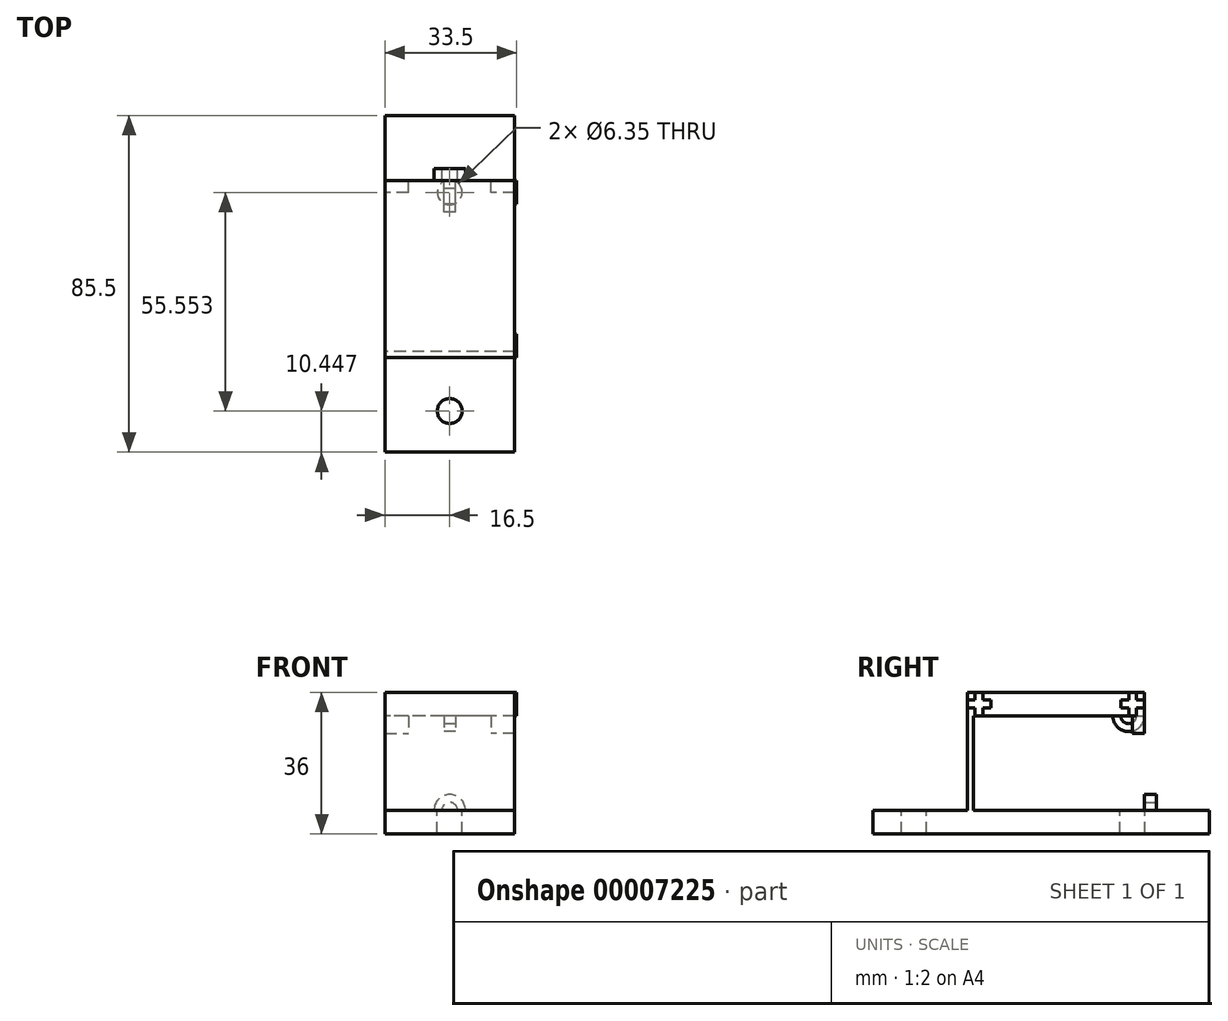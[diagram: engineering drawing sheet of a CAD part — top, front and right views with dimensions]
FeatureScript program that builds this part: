
annotation { "Feature Type Name" : "Feature", "Feature Type Description" : "" }
export const myFeature = defineFeature(function(context is Context, id is Id, definition is map)
    precondition{}
    {
        {
            var Q0;
            Q0=qCreatedBy(makeId("Right.planeOp"),FACE);
            var sketch = newSketch(context, id + "F0", { "sketchPlane" : qUnion([Q0])});
            skLineSegment(sketch, "E0", {"start": v(1.5, 30) * mm, "end": v(42, 30) * mm});
            skLineSegment(sketch, "E1", {"start": v(45, 30) * mm, "end": v(45, 36) * mm});
            skLineSegment(sketch, "E2", {"start": v(45, 36) * mm, "end": v(0, 36) * mm});
            skLineSegment(sketch, "E3", {"start": v(0, 36) * mm, "end": v(0, 6) * mm});
            skLineSegment(sketch, "E4", {"start": v(0, 0) * mm, "end": v(61.5, 0) * mm});
            skLineSegment(sketch, "E5", {"start": v(1.5, 30) * mm, "end": v(1.5, 6) * mm});
            skLineSegment(sketch, "E6", {"start": v(1.5, 6) * mm, "end": v(61.5, 6) * mm});
            skLineSegment(sketch, "E7", {"start": v(61.5, 6) * mm, "end": v(61.5, 0) * mm});
            skPoint(sketch, "E8", {"position": v(42, 30) * mm});
            skPoint(sketch, "E9", {"position": v(0, 30) * mm});
            skPoint(sketch, "E10", {"position": v(0, 6) * mm});
            skLineSegment(sketch, "E11", {"start": v(0, 6) * mm, "end": v(-24, 6) * mm});
            skLineSegment(sketch, "E12", {"start": v(-24, 6) * mm, "end": v(-24, 0) * mm});
            skLineSegment(sketch, "E13", {"start": v(-24, 0) * mm, "end": v(0, 0) * mm});
            skPoint(sketch, "E14.end.orphan", {"position": v(45, 22.38) * mm});
            skLineSegment(sketch, "E15", {"start": v(42, 30) * mm, "end": v(45, 30) * mm});
            skSolve(sketch);
        }
        {
            var Q0;
            Q0=qSketchRegion(id+"F0",true);
            extrude(context, id + "F1", {"entities" : qUnion([Q0]), "depth" : 33 * mm});
        }
        {
            var Q0;
            Q0=makeQuery(id+"F1.opExtrude","CAP_FACE",FACE,{"disambiguationData":[OSD([sQuery(id+"F0.wireOp",EDGE,"E0"),sQuery(id+"F0.wireOp",EDGE,"E1"),sQuery(id+"F0.wireOp",EDGE,"E2"),sQuery(id+"F0.wireOp",EDGE,"E3"),sQuery(id+"F0.wireOp",EDGE,"E4"),sQuery(id+"F0.wireOp",EDGE,"E5"),sQuery(id+"F0.wireOp",EDGE,"E6"),sQuery(id+"F0.wireOp",EDGE,"E7"),sQuery(id+"F0.wireOp",EDGE,"E11"),sQuery(id+"F0.wireOp",EDGE,"E12"),sQuery(id+"F0.wireOp",EDGE,"E13"),sQuery(id+"F0.wireOp",EDGE,"E15")])],"isStart":false});
            var sketch = newSketch(context, id + "F2", { "sketchPlane" : qUnion([Q0])});
            skArc(sketch, "E16", {"start": v(37, 30) * mm, "mid": v(41, 26) * mm, "end": v(45, 30) * mm});
            skArc(sketch, "E17", {"start": v(39, 30) * mm, "mid": v(41, 28) * mm, "end": v(43, 30) * mm});
            skLineSegment(sketch, "E18", {"start": v(39, 30) * mm, "end": v(37, 30) * mm});
            skLineSegment(sketch, "E19", {"start": v(37, 30) * mm, "end": v(39, 30) * mm});
            skLineSegment(sketch, "E20", {"start": v(43, 30) * mm, "end": v(45, 30) * mm});
            skSolve(sketch);
        }
        {
            var Q0;
            Q0 = qSketchRegion(id + "F2", true);
            extrude(context, id + "F3", {"entities" : qUnion([Q0]), "depth" : 3 * mm});
        }
        {
            var Q0;
            Q0=makeQuery(id+"F3.opExtrude","SWEPT_BODY",BODY,{"disambiguationData":[OSD([sQuery(id+"F2.wireOp",EDGE,"E16"),sQuery(id+"F2.wireOp",EDGE,"E17"),sQuery(id+"F2.wireOp",EDGE,"E19"),sQuery(id+"F2.wireOp",EDGE,"E20")])]});
            var Q1;
            Q1=makeQuery(id+"F1.opExtrude","SWEPT_EDGE",EDGE,{"disambiguationData":[OSD([sQuery(id+"F0.wireOp",EDGE,"E1"),sQuery(id+"F0.wireOp",EDGE,"E15")])]});
            transform(context, id + "F4", {"entities" : qUnion([Q0]), "transformType" : TransformType.TRANSLATION_DISTANCE, "transformDirection" : qUnion([Q1]), "distance" : 18 * mm, "makeCopy" : false});
        }
        {
            var Q0;
            Q0=makeQuery(id+"F1.opExtrude","SWEPT_FACE",FACE,{"disambiguationData":[OSD([sQuery(id+"F0.wireOp",EDGE,"E7")])]});
            var sketch = newSketch(context, id + "F5", { "sketchPlane" : qUnion([Q0])});
            skArc(sketch, "E21", {"start": v(-12.5, 6) * mm, "mid": v(-16.5, 10) * mm, "end": v(-20.5, 6) * mm});
            skArc(sketch, "E22", {"start": v(-14.5, 6) * mm, "mid": v(-16.5, 8) * mm, "end": v(-18.5, 6) * mm});
            skLineSegment(sketch, "E23", {"start": v(-20.5, 6) * mm, "end": v(-18.5, 6) * mm});
            skLineSegment(sketch, "E24", {"start": v(-14.5, 6) * mm, "end": v(-12.5, 6) * mm});
            skSolve(sketch);
        }
        {
            var Q0;
            Q0 = qSketchRegion(id + "F5", true);
            extrude(context, id + "F6", {"entities" : qUnion([Q0]), "oppositeDirection" : true, "depth" : 3 * mm});
        }
        {
            var Q0;
            Q0=makeQuery(id+"F6.opExtrude","SWEPT_BODY",BODY,{"disambiguationData":[OSD([sQuery(id+"F5.wireOp",EDGE,"E21"),sQuery(id+"F5.wireOp",EDGE,"E22"),sQuery(id+"F5.wireOp",EDGE,"E23"),sQuery(id+"F5.wireOp",EDGE,"E24")])]});
            var Q1;
            Q1=makeQuery(id+"F1.opExtrude","CAP_EDGE",EDGE,{"disambiguationData":[OSD([sQuery(id+"F0.wireOp",EDGE,"E6")])],"isStart":false});
            transform(context, id + "F7", {"entities" : qUnion([Q0]), "transformType" : TransformType.TRANSLATION_DISTANCE, "transformDirection" : qUnion([Q1]), "distance" : 13.5 * mm, "oppositeDirection" : true, "makeCopy" : false});
        }
        {
            var Q0;
            Q0=makeQuery(id+"F1.opExtrude","SWEPT_FACE",FACE,{"disambiguationData":[OSD([sQuery(id+"F0.wireOp",EDGE,"E1")])]});
            var sketch = newSketch(context, id + "F8", { "sketchPlane" : qUnion([Q0])});
            skLineSegment(sketch, "E25.bottom", {"start": v(-33, 30) * mm, "end": v(-27, 30) * mm});
            skLineSegment(sketch, "E25.top", {"start": v(-33, 25.5) * mm, "end": v(-27, 25.5) * mm});
            skLineSegment(sketch, "E25.left", {"start": v(-33, 30) * mm, "end": v(-33, 25.5) * mm});
            skLineSegment(sketch, "E25.right", {"start": v(-27, 30) * mm, "end": v(-27, 25.5) * mm});
            skLineSegment(sketch, "E26.bottom", {"start": v(0, 30) * mm, "end": v(-6, 30) * mm});
            skLineSegment(sketch, "E26.top", {"start": v(0, 25.5) * mm, "end": v(-6, 25.5) * mm});
            skLineSegment(sketch, "E26.left", {"start": v(0, 30) * mm, "end": v(0, 25.5) * mm});
            skLineSegment(sketch, "E26.right", {"start": v(-6, 30) * mm, "end": v(-6, 25.5) * mm});
            skLineSegment(sketch, "E27", {"start": v(-16.5, 30) * mm, "end": v(-16.5, 12.44) * mm, "construction": true});
            skSolve(sketch);
        }
        {
            var Q0;
            Q0 = qSketchRegion(id + "F8", true);
            extrude(context, id + "F9", {"entities" : qUnion([Q0]), "oppositeDirection" : true, "depth" : 3 * mm});
        }
        {
            var Q0;
            Q0=makeQuery(id+"F1.opExtrude","SWEPT_BODY",BODY,{"disambiguationData":[OSD([sQuery(id+"F0.wireOp",EDGE,"E0"),sQuery(id+"F0.wireOp",EDGE,"E1"),sQuery(id+"F0.wireOp",EDGE,"E2"),sQuery(id+"F0.wireOp",EDGE,"E3"),sQuery(id+"F0.wireOp",EDGE,"E4"),sQuery(id+"F0.wireOp",EDGE,"E5"),sQuery(id+"F0.wireOp",EDGE,"E6"),sQuery(id+"F0.wireOp",EDGE,"E7"),sQuery(id+"F0.wireOp",EDGE,"E11"),sQuery(id+"F0.wireOp",EDGE,"E12"),sQuery(id+"F0.wireOp",EDGE,"E13"),sQuery(id+"F0.wireOp",EDGE,"E15")])]});
            var Q1;
            Q1=makeQuery(id+"F3.opExtrude","SWEPT_BODY",BODY,{"disambiguationData":[OSD([sQuery(id+"F2.wireOp",EDGE,"E16"),sQuery(id+"F2.wireOp",EDGE,"E17"),sQuery(id+"F2.wireOp",EDGE,"E19"),sQuery(id+"F2.wireOp",EDGE,"E20")])]});
            var Q2;
            Q2=makeQuery(id+"F9.opExtrude","SWEPT_BODY",BODY,{"disambiguationData":[OSD([sQuery(id+"F8.wireOp",EDGE,"E26.bottom"),sQuery(id+"F8.wireOp",EDGE,"E26.top"),sQuery(id+"F8.wireOp",EDGE,"E26.left"),sQuery(id+"F8.wireOp",EDGE,"E26.right")])]});
            var Q3;
            Q3=makeQuery(id+"F9.opExtrude","SWEPT_BODY",BODY,{"disambiguationData":[OSD([sQuery(id+"F8.wireOp",EDGE,"E25.bottom"),sQuery(id+"F8.wireOp",EDGE,"E25.top"),sQuery(id+"F8.wireOp",EDGE,"E25.left"),sQuery(id+"F8.wireOp",EDGE,"E25.right")])]});
            var Q4;
            Q4=makeQuery(id+"F6.opExtrude","SWEPT_BODY",BODY,{"disambiguationData":[OSD([sQuery(id+"F5.wireOp",EDGE,"E21"),sQuery(id+"F5.wireOp",EDGE,"E22"),sQuery(id+"F5.wireOp",EDGE,"E23"),sQuery(id+"F5.wireOp",EDGE,"E24")])]});
            booleanBodies(context, id + "F10", {"operationType" : BooleanOperationType.UNION, "tools" : qUnion([Q0, Q1, Q2, Q3, Q4])});
        }
        {
            var Q0;
            Q0=makeQuery(id+"F10.opBoolean","MERGE",FACE,{"derivedFrom":[makeQuery(id+"F1.opExtrude","CAP_FACE",FACE,{"disambiguationData":[OSD([sQuery(id+"F0.wireOp",EDGE,"E0"),sQuery(id+"F0.wireOp",EDGE,"E1"),sQuery(id+"F0.wireOp",EDGE,"E2"),sQuery(id+"F0.wireOp",EDGE,"E3"),sQuery(id+"F0.wireOp",EDGE,"E4"),sQuery(id+"F0.wireOp",EDGE,"E5"),sQuery(id+"F0.wireOp",EDGE,"E6"),sQuery(id+"F0.wireOp",EDGE,"E7"),sQuery(id+"F0.wireOp",EDGE,"E11"),sQuery(id+"F0.wireOp",EDGE,"E12"),sQuery(id+"F0.wireOp",EDGE,"E13"),sQuery(id+"F0.wireOp",EDGE,"E15")])],"isStart":false}),makeQuery(id+"F9.opExtrude","SWEPT_FACE",FACE,{"disambiguationData":[OSD([sQuery(id+"F8.wireOp",EDGE,"E25.left")])]})]});
            var sketch = newSketch(context, id + "F11", { "sketchPlane" : qUnion([Q0])});
            skLineSegment(sketch, "E28", {"start": v(22.5, 36) * mm, "end": v(22.5, 30) * mm, "construction": true});
            skLineSegment(sketch, "E29.bottom", {"start": v(0, 34) * mm, "end": v(2, 34) * mm});
            skLineSegment(sketch, "E29.top", {"start": v(0, 32) * mm, "end": v(2, 32) * mm});
            skLineSegment(sketch, "E29.left", {"start": v(0, 34) * mm, "end": v(0, 32) * mm});
            skLineSegment(sketch, "E29.right", {"start": v(6, 34) * mm, "end": v(6, 32) * mm});
            skLineSegment(sketch, "E30.bottom", {"start": v(39, 34) * mm, "end": v(41, 34) * mm});
            skLineSegment(sketch, "E30.top", {"start": v(39, 32) * mm, "end": v(41, 32) * mm});
            skLineSegment(sketch, "E30.left", {"start": v(39, 34) * mm, "end": v(39, 32) * mm});
            skLineSegment(sketch, "E30.right", {"start": v(45, 34) * mm, "end": v(45, 32) * mm});
            skLineSegment(sketch, "E31.bottom", {"start": v(2, 36) * mm, "end": v(4, 36) * mm});
            skLineSegment(sketch, "E31.top", {"start": v(2, 30) * mm, "end": v(4, 30) * mm});
            skLineSegment(sketch, "E31.left", {"start": v(2, 36) * mm, "end": v(2, 34) * mm});
            skLineSegment(sketch, "E31.right", {"start": v(4, 36) * mm, "end": v(4, 34) * mm});
            skLineSegment(sketch, "E32.bottom", {"start": v(41, 36) * mm, "end": v(43, 36) * mm});
            skLineSegment(sketch, "E32.top", {"start": v(41, 30) * mm, "end": v(43, 30) * mm});
            skLineSegment(sketch, "E32.left", {"start": v(41, 36) * mm, "end": v(41, 34) * mm});
            skLineSegment(sketch, "E32.right", {"start": v(43, 36) * mm, "end": v(43, 34) * mm});
            skPoint(sketch, "E33", {"position": v(2, 34) * mm});
            skPoint(sketch, "E34", {"position": v(4, 34) * mm});
            skPoint(sketch, "E35", {"position": v(4, 32) * mm});
            skPoint(sketch, "E36", {"position": v(2, 32) * mm});
            skPoint(sketch, "E37", {"position": v(41, 34) * mm});
            skPoint(sketch, "E38", {"position": v(43, 34) * mm});
            skPoint(sketch, "E39", {"position": v(43, 32) * mm});
            skPoint(sketch, "E40", {"position": v(41, 32) * mm});
            skLineSegment(sketch, "E41.trimOffspring", {"start": v(4, 32) * mm, "end": v(4, 30) * mm});
            skLineSegment(sketch, "E42.trimOffspring", {"start": v(4, 34) * mm, "end": v(6, 34) * mm});
            skLineSegment(sketch, "E43.trimOffspring", {"start": v(2, 32) * mm, "end": v(2, 30) * mm});
            skLineSegment(sketch, "E44.trimOffspring", {"start": v(4, 32) * mm, "end": v(6, 32) * mm});
            skLineSegment(sketch, "E45.trimOffspring", {"start": v(43, 34) * mm, "end": v(45, 34) * mm});
            skLineSegment(sketch, "E46.trimOffspring", {"start": v(41, 32) * mm, "end": v(41, 30) * mm});
            skLineSegment(sketch, "E47.trimOffspring", {"start": v(43, 32) * mm, "end": v(45, 32) * mm});
            skLineSegment(sketch, "E48.trimOffspring", {"start": v(43, 32) * mm, "end": v(43, 30) * mm});
            skSolve(sketch);
        }
        {
            var Q0;
            Q0 = qSketchRegion(id + "F11", true);
            extrude(context, id + "F12", {"entities" : qUnion([Q0]), "depth" : 0.5 * mm});
        }
        {
            var Q0;
            Q0=makeQuery(id+"F1.opExtrude","SWEPT_FACE",FACE,{"disambiguationData":[OSD([sQuery(id+"F0.wireOp",EDGE,"E6")])]});
            var sketch = newSketch(context, id + "F13", { "sketchPlane" : qUnion([Q0])});
            skLineSegment(sketch, "E49", {"start": v(16.5, 61.5) * mm, "end": v(16.5, -23.71) * mm, "construction": true});
            skCircle(sketch, "E50", {"center": v(16.5, 42) * mm, "radius": 3.18 * mm});
            skCircle(sketch, "E51", {"center": v(16.5, -13.55) * mm, "radius": 3.18 * mm});
            skSolve(sketch);
        }
        {
            var Q0;
            Q0 = qSketchRegion(id + "F13", true);
            extrude(context, id + "F14", {"entities" : qUnion([Q0]), "operationType" : NewBodyOperationType.REMOVE, "oppositeDirection" : true, "depth" : 6 * mm});
        }
    });
